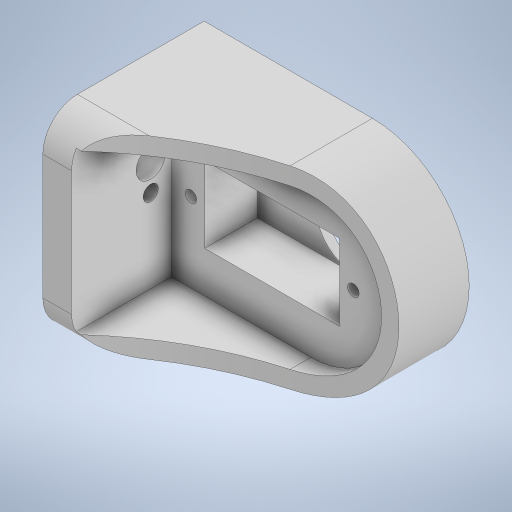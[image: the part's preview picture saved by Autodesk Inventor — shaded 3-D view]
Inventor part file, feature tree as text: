
AUTODESK INVENTOR PART (.ipt)
format: ipt  version: 2024.1 (Build 281209000, 209)  size: 325,632 bytes
history: native  units: in
note: dims shown in document units (in); Inventor stores cm internally (conversion verified against a paired STEP export)
features: extrude x6, sketch x6, fillet x1
ambient origin geometry x8: Origin, YZ Plane, XZ Plane, XY Plane, X Axis, Y Axis, Z Axis, Center Point
bodies: Solid1 (feature_tree)
feature tree (13):
  extrude  "Extrusion1"  Depth=3.3071in
  extrude  "Extrusion2"  Depth=1.2992in
  extrude  "Extrusion3"  Depth=0.2953in
  fillet  "Fillet1"  Radius=0.4921in
  extrude  "Extrusion4"  Depth=1.2008in
  extrude  "Extrusion5"  Depth=0.2953in
  extrude  "Extrusion6"  Depth=0.7992in
  sketch  "Sketch1"  dims[d0=4.5276in d1=3.3071in]
  sketch  "Sketch2"  dims[d2=1.2992in d3=1.811in]
  sketch  "Sketch3"  dims[d4=2.7559in d5=0.0in d6=0.2953in d7=0.4921in]
  sketch  "Sketch4"  dims[d8=1.7047in d9=0.0in d10=1.2008in]
  sketch  "Sketch5"  dims[d11=0.4921in d12=0.2953in]
  sketch  "Sketch6"  dims[d13=0.0in d14=0.0in d15=0.5906in d16=0.3543in d17=0.5in d18=1.1417in d19=0.2598in d20=0.4488in d21=0.2598in d22=0.4488in d23=0.0in d24=0.0in d25=2.3031in d26=0.8976in d27=0.0in d28=0.1969in d29=0.2362in d30=0.7992in d31=0.0in]
